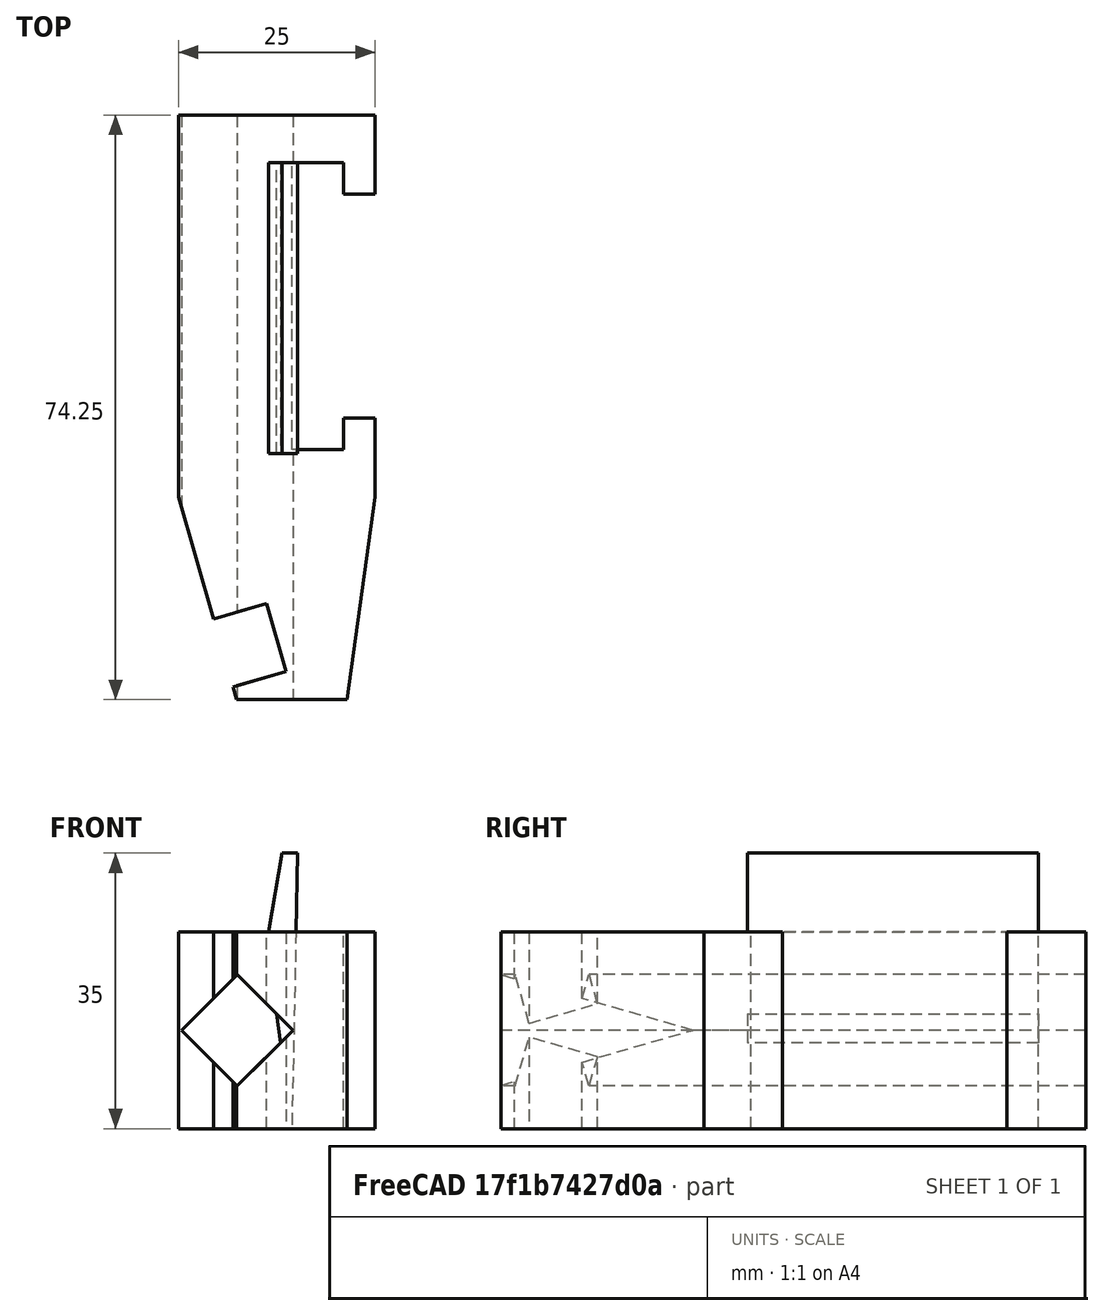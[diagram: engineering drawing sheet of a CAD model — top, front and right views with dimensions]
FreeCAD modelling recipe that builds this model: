
FCSTD DOCUMENT  (FreeCAD 0.19R)
Label: disherend
License: All rights reserved
LicenseURL: http://en.wikipedia.org/wiki/All_rights_reserved
objects: Sketcher::SketchObject×6, PartDesign::Pocket×3, PartDesign::Pad×2, PartDesign::Body×1, Mesh::Feature×1
note: 17 computed .brp shape members not serialized (recipe doc carries the construction recipe); baked Part::Feature solids carry a one-line shape summary decoded from their .brp

FEATURE [Sketcher::SketchObject] Sketch
  FullyConstrained = true
  MapMode = 5
  Support = -> [XY_Plane]
  sketch-geometry (14):
    g0: LineSegment StartX=0 StartY=-18.25 StartZ=0 EndX=0 EndY=18.25 EndZ=0
    g1: LineSegment StartX=0 StartY=18.25 StartZ=0 EndX=6.6 EndY=18.25 EndZ=0
    g2: LineSegment StartX=6.6 StartY=18.25 StartZ=0 EndX=6.6 EndY=14.25 EndZ=0
    g3: LineSegment StartX=6.6 StartY=14.25 StartZ=0 EndX=10.6 EndY=14.25 EndZ=0
    g4: LineSegment StartX=10.6 StartY=14.25 StartZ=0 EndX=10.6 EndY=24.25 EndZ=0
    g5: LineSegment StartX=10.6 StartY=24.25 StartZ=0 EndX=-14.4 EndY=24.25 EndZ=0
    g6: LineSegment StartX=-14.4 StartY=24.25 StartZ=0 EndX=-14.4 EndY=-24.25 EndZ=0
    g7: LineSegment StartX=10.6 StartY=-24.25 StartZ=0 EndX=10.6 EndY=-14.25 EndZ=0
    g8: LineSegment StartX=10.6 StartY=-14.25 StartZ=0 EndX=6.6 EndY=-14.25 EndZ=0
    g9: LineSegment StartX=6.6 StartY=-14.25 StartZ=0 EndX=6.6 EndY=-18.25 EndZ=0
    g10: LineSegment StartX=6.6 StartY=-18.25 StartZ=0 EndX=0 EndY=-18.25 EndZ=0
    g11: LineSegment StartX=-14.4 StartY=-24.25 StartZ=0 EndX=-7 EndY=-50 EndZ=0
    g12: LineSegment StartX=-7 StartY=-50 StartZ=0 EndX=7 EndY=-50 EndZ=0
    g13: LineSegment StartX=7 StartY=-50 StartZ=0 EndX=10.6 EndY=-24.25 EndZ=0
  constraints (37):
    c: PointOnObject(g0,g-2)
    c: Coincident(g0,g1)
    c: Horizontal(g1)
    c: Coincident(g1,g2)
    c: Coincident(g2,g3)
    c: Horizontal(g3)
    c: Coincident(g3,g4)
    c: Vertical(g4)
    c: Coincident(g4,g5)
    c: Coincident(g5,g6)
    c: Coincident(g7,g8)
    c: Coincident(g8,g9)
    c: Vertical(g9)
    c: Coincident(g9,g10)
    c: Coincident(g10,g0)
    c: Symmetric(g6,g5,g-1)
    c: Symmetric(g7,g4,g-1)
    c: Symmetric(g0,g0,g-1)
    c: Distance(g0) = 36.5
    c: Horizontal(g10)
    c: Equal(g10,g1)
    c: Distance(g1) = 6.6
    c: Vertical(g2)
    c: Horizontal(g8)
    c: Symmetric(g7,g3,g-1)
    c: Distance(g9) = 4
    c: Distance(g8) = 4
    c: Horizontal(g5)
    c: Distance(g7) = 10
    c: Distance(g5) = 25
    c: Coincident(g6,g11)
    c: Coincident(g11,g12)
    c: Coincident(g12,g13)
    c: Coincident(g13,g7)
    c: Symmetric(g12,g11,g-2)
    c: Distance(g12) = 14
    c: DistanceY(g12) = -50
FEATURE [PartDesign::Pad] Pad
  Direction = (1,1,1)
  Length = 25
  Length2 = 100
  Profile = -> Sketch
  Type = 0
FEATURE [Sketcher::SketchObject] Sketch001
  FullyConstrained = true
  MapMode = 5
  Placement = pos=(0,24.25,0) rot=(0,0.707107,0.707107;3.14159rad)
  Support = -> [Pad]
  sketch-geometry (4):
    g0: LineSegment StartX=6.92893 StartY=19.5711 StartZ=0 EndX=-0.142136 EndY=12.5 EndZ=0
    g1: LineSegment StartX=-0.142136 StartY=12.5 StartZ=0 EndX=6.92893 EndY=5.42893 EndZ=0
    g2: LineSegment StartX=6.92893 StartY=5.42893 StartZ=0 EndX=14 EndY=12.5 EndZ=0
    g3: LineSegment StartX=14 StartY=12.5 StartZ=0 EndX=6.92893 EndY=19.5711 EndZ=0
  constraints (12):
    c: Coincident(g0,g1)
    c: Coincident(g1,g2)
    c: Coincident(g2,g3)
    c: Coincident(g3,g0)
    c: Distance(g2) = 10
    c: Equal(g2,g3)
    c: Equal(g3,g0)
    c: Equal(g1,g0)
    c: Perpendicular(g0,g3)
    c: DistanceY(g2) = 12.5
    c: DistanceY(g0) = 12.5
    c: DistanceX(g2) = 14
FEATURE [PartDesign::Pocket] Pocket
  BaseFeature = -> Pad
  Length = 5
  Length2 = 100
  Profile = -> Sketch001
  Type = 1
FEATURE [Sketcher::SketchObject] Sketch002
  ExternalGeometry = -> [Pocket]
  FullyConstrained = false
  MapMode = 5
  Placement = pos=(0,18.25,0) rot=(1,0,0;1.5708rad)
  Support = -> [Pocket]
  sketch-geometry (4):
    g0: LineSegment StartX=0 StartY=-3.6e-15 StartZ=0 EndX=0.75 EndY=35 EndZ=0
    g1: LineSegment StartX=0.75 StartY=35 StartZ=0 EndX=-1.25 EndY=35 EndZ=0
    g2: LineSegment StartX=-1.25 StartY=35 StartZ=0 EndX=-3.13081 EndY=23.8315 EndZ=0
    g3: LineSegment StartX=-3.13081 StartY=23.8315 StartZ=0 EndX=0 EndY=-3.6e-15 EndZ=0
  constraints (9):
    c: Coincident(g-3,g0)
    c: Coincident(g0,g1)
    c: Horizontal(g1)
    c: Coincident(g1,g2)
    c: Coincident(g2,g3)
    c: Coincident(g3,g0)
    c: Distance(g1) = 2
    c: DistanceX(g-1,g0) = 0.75
    c: DistanceY(g0) = 35
FEATURE [PartDesign::Pad] Pad001
  BaseFeature = -> Pocket
  Direction = (1,1,1)
  Length = 37
  Length2 = 100
  Profile = -> Sketch002
  Type = 0
FEATURE [Sketcher::SketchObject] Sketch003
  FullyConstrained = false
  MapMode = 5
  Placement = pos=(-1.5e-14,18.25,-1e-15) rot=(0,0.707107,0.707107;3.14159rad)
  sketch-geometry (4):
    g0: LineSegment StartX=0 StartY=16.2446 StartZ=0 EndX=-4.24264 EndY=12.002 EndZ=0
    g1: LineSegment StartX=-4.24264 StartY=12.002 StartZ=0 EndX=0 EndY=7.75933 EndZ=0
    g2: LineSegment StartX=0 StartY=7.75933 StartZ=0 EndX=4.24264 EndY=12.002 EndZ=0
    g3: LineSegment StartX=4.24264 StartY=12.002 StartZ=0 EndX=0 EndY=16.2446 EndZ=0
  constraints (11):
    c: PointOnObject(g0,g-2)
    c: Coincident(g0,g1)
    c: PointOnObject(g1,g-2)
    c: Coincident(g1,g2)
    c: Coincident(g2,g3)
    c: Coincident(g3,g0)
    c: Equal(g0,g1)
    c: Equal(g1,g2)
    c: Equal(g2,g3)
    c: Perpendicular(g0,g3)
    c: Distance(g3) = 6
FEATURE [Sketcher::SketchObject] Sketch004
  FullyConstrained = false
  MapMode = 5
  Placement = pos=(-19.7388,-5.6725,0) rot=(0.684497,-0.515492,-0.515492;1.9411rad)
  Support = -> [Pad001]
  sketch-geometry (5):
    g0: LineSegment StartX=54 StartY=41.3236 StartZ=0 EndX=59 EndY=12.5 EndZ=0
    g1: LineSegment StartX=59 StartY=12.5 StartZ=0 EndX=54 EndY=-17.5224 EndZ=0
    g2: LineSegment StartX=54 StartY=-17.5224 StartZ=0 EndX=94.9088 EndY=-20.9534 EndZ=0
    g3: LineSegment StartX=94.9088 StartY=-20.9534 StartZ=0 EndX=94.9088 EndY=46.3218 EndZ=0
    g4: LineSegment StartX=94.9088 StartY=46.3218 StartZ=0 EndX=54 EndY=41.3236 EndZ=0
  constraints (10):
    c: Coincident(g0,g1)
    c: Coincident(g1,g2)
    c: Coincident(g2,g3)
    c: Vertical(g3)
    c: Coincident(g3,g4)
    c: Coincident(g4,g0)
    c: DistanceY(g0) = 12.5
    c: DistanceX(g0) = 54
    c: DistanceX(g1) = 54
    c: DistanceX(g0) = 59
FEATURE [PartDesign::Pocket] Pocket001
  BaseFeature = -> Pad001
  Length = 19
  Length2 = 100
  Profile = -> Sketch004
  Type = 0
FEATURE [Sketcher::SketchObject] Sketch005
  FullyConstrained = false
  MapMode = 5
  Placement = pos=(-19.7388,-5.6725,0) rot=(0.684497,-0.515492,-0.515492;1.9411rad)
  Support = -> [Pocket001]
  sketch-geometry (4):
    g0: LineSegment StartX=44.4401 StartY=28.5651 StartZ=0 EndX=44.4401 EndY=-4.23629 EndZ=0
    g1: LineSegment StartX=44.4401 StartY=-4.23629 StartZ=0 EndX=35.4429 EndY=-4.5936 EndZ=0
    g2: LineSegment StartX=35.4429 StartY=-4.5936 StartZ=0 EndX=35.4429 EndY=29.1368 EndZ=0
    g3: LineSegment StartX=35.4429 StartY=29.1368 StartZ=0 EndX=44.4401 EndY=28.5651 EndZ=0
  constraints (6):
    c: Vertical(g0)
    c: Coincident(g0,g1)
    c: Coincident(g1,g2)
    c: Vertical(g2)
    c: Coincident(g2,g3)
    c: Coincident(g3,g0)
FEATURE [PartDesign::Pocket] Pocket002
  BaseFeature = -> Pocket001
  Length = 7
  Length2 = 100
  Profile = -> Sketch005
  Type = 0
FEATURE [PartDesign::Body] Body
  Group = -> [Sketch,Pad,Sketch001,Pocket,Sketch002,Pad001,Sketch003,Sketch004,Pocket001,Sketch005,Pocket002]
  Origin = -> Origin
  Tip = -> Pocket002
FEATURE [Mesh::Feature] Mesh  label="Pocket002 (Meshed)"
